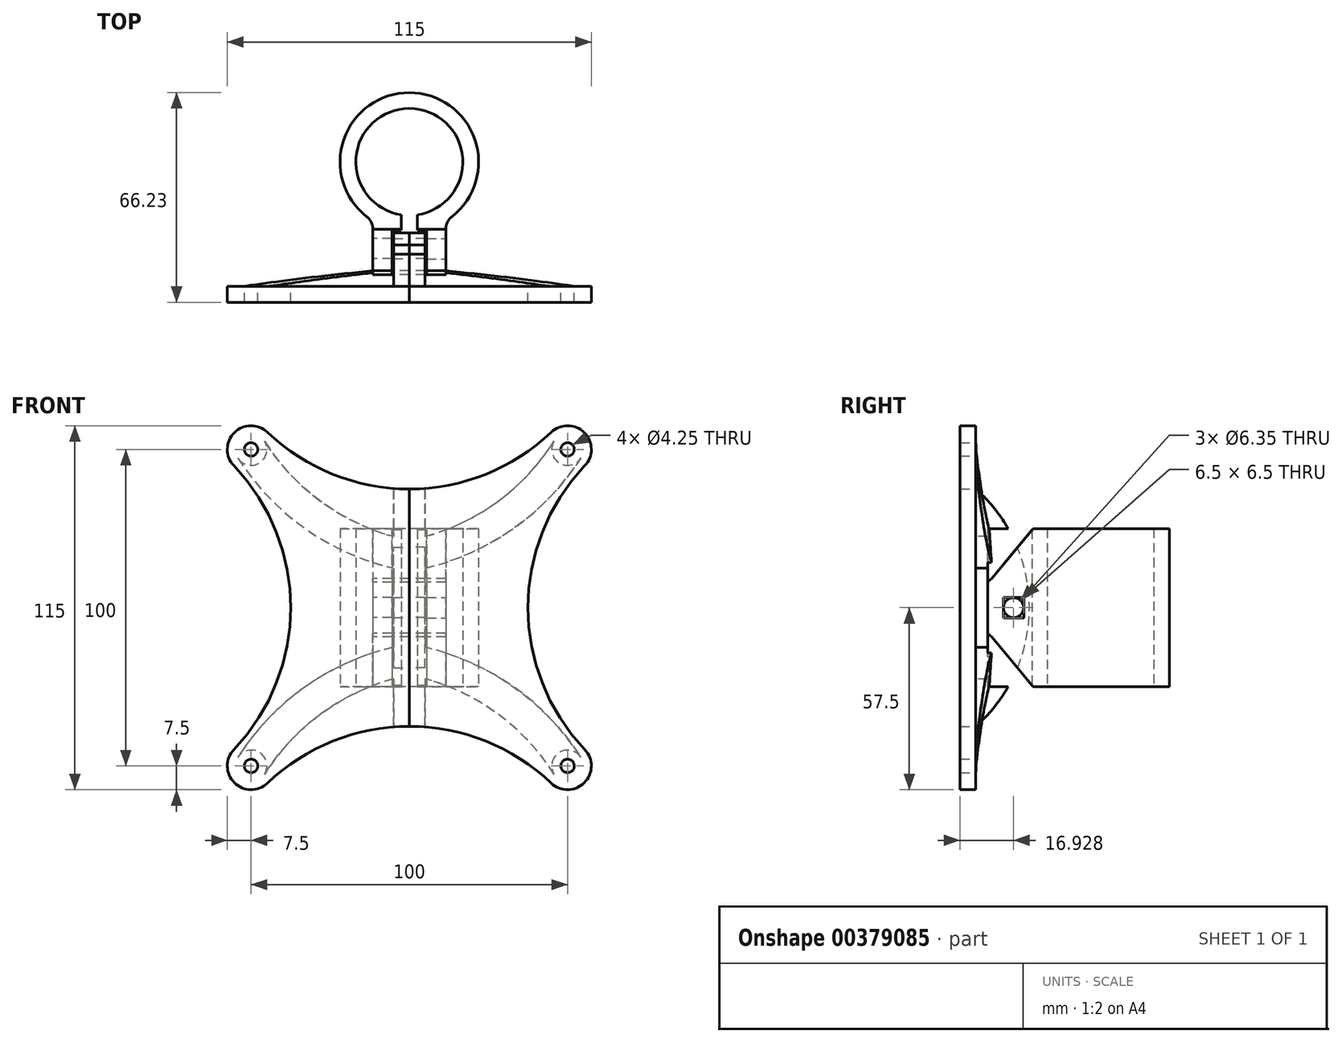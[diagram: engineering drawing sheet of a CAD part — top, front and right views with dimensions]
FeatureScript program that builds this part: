
annotation { "Feature Type Name" : "Feature", "Feature Type Description" : "" }
export const myFeature = defineFeature(function(context is Context, id is Id, definition is map)
    precondition{}
    {
        {
            var Q0;
            Q0=qCreatedBy(makeId("Front.planeOp"),FACE);
            var sketch = newSketch(context, id + "F0", { "sketchPlane" : qUnion([Q0])});
            skLineSegment(sketch, "E0.bottom", {"start": v(50, 50) * mm, "end": v(-50, 50) * mm, "construction": true});
            skLineSegment(sketch, "E0.top", {"start": v(50, -50) * mm, "end": v(-50, -50) * mm, "construction": true});
            skLineSegment(sketch, "E0.left", {"start": v(50, 50) * mm, "end": v(50, -50) * mm, "construction": true});
            skLineSegment(sketch, "E0.right", {"start": v(-50, 50) * mm, "end": v(-50, -50) * mm, "construction": true});
            skPoint(sketch, "E0.middle", {"position": v(0, 0) * mm});
            skCircle(sketch, "E1", {"center": v(-50, 50) * mm, "radius": 2.12 * mm});
            skCircle(sketch, "E2", {"center": v(50, 50) * mm, "radius": 2.12 * mm});
            skCircle(sketch, "E3", {"center": v(-50, -50) * mm, "radius": 2.12 * mm});
            skCircle(sketch, "E4", {"center": v(50, -50) * mm, "radius": 2.12 * mm});
            skArc(sketch, "E5", {"start": v(-44.83, 55.43) * mm, "mid": v(-55.3, 55.3) * mm, "end": v(-55.43, 44.83) * mm});
            skArc(sketch, "E6", {"start": v(55.43, 44.83) * mm, "mid": v(55.3, 55.3) * mm, "end": v(44.83, 55.43) * mm});
            skArc(sketch, "E7", {"start": v(44.83, -55.43) * mm, "mid": v(55.3, -55.3) * mm, "end": v(55.43, -44.83) * mm});
            skArc(sketch, "E8", {"start": v(-55.43, -44.83) * mm, "mid": v(-55.3, -55.3) * mm, "end": v(-44.83, -55.43) * mm});
            skLineSegment(sketch, "E9.bottom", {"start": v(37.5, 37.5) * mm, "end": v(-37.5, 37.5) * mm, "construction": true});
            skLineSegment(sketch, "E9.top", {"start": v(37.5, -37.5) * mm, "end": v(-37.5, -37.5) * mm, "construction": true});
            skLineSegment(sketch, "E9.left", {"start": v(37.5, 37.5) * mm, "end": v(37.5, -37.5) * mm, "construction": true});
            skLineSegment(sketch, "E9.right", {"start": v(-37.5, 37.5) * mm, "end": v(-37.5, -37.5) * mm, "construction": true});
            skArc(sketch, "E10", {"start": v(-44.83, 55.43) * mm, "mid": v(0, 37.5) * mm, "end": v(44.83, 55.43) * mm});
            skArc(sketch, "E11", {"start": v(44.83, -55.43) * mm, "mid": v(0, -37.5) * mm, "end": v(-44.83, -55.43) * mm});
            skArc(sketch, "E12", {"start": v(-55.43, -44.83) * mm, "mid": v(-37.5, 0) * mm, "end": v(-55.43, 44.83) * mm});
            skArc(sketch, "E13", {"start": v(55.43, 44.83) * mm, "mid": v(37.5, 0) * mm, "end": v(55.43, -44.83) * mm});
            skLineSegment(sketch, "E14", {"start": v(0, 37.5) * mm, "end": v(0, -37.5) * mm});
            skSolve(sketch);
        }
        {
            var Q0;
            Q0=makeQuery(id+"F0.imprint","IMPRINT",FACE,{"disambiguationData":[TD([[makeQuery(id+"F0.imprint","IMPRINT",EDGE,{"derivedFrom":sQuery(id+"F0.wireOp",EDGE,"E1")}),-1.0]])]});
            extrude(context, id + "F1", {"entities" : qUnion([Q0]), "depth" : 5 * mm, "offsetDistance" : 25 * mm});
        }
        {
            var Q0;
            Q0=qCreatedBy(makeId("Right.planeOp"),FACE);
            var sketch = newSketch(context, id + "F2", { "sketchPlane" : qUnion([Q0])});
            skLineSegment(sketch, "E15.0", {"start": v(0, 37.5) * mm, "end": v(0, -37.5) * mm});
            skArc(sketch, "E16", {"start": v(0, -37.5) * mm, "mid": v(16.93, 0) * mm, "end": v(0, 37.5) * mm});
            skLineSegment(sketch, "E17", {"start": v(0, 0) * mm, "end": v(16.93, 0) * mm, "construction": true});
            skCircle(sketch, "E18", {"center": v(11.93, 0) * mm, "radius": 3.17 * mm});
            skSolve(sketch);
        }
        {
            var Q0;
            Q0=makeQuery(id+"F2.imprint","IMPRINT",FACE,{"disambiguationData":[TD([[makeQuery(id+"F2.imprint","IMPRINT",EDGE,{"derivedFrom":sQuery(id+"F2.wireOp",EDGE,"E15.0")}),1.0]])]});
            extrude(context, id + "F3", {"entities" : qUnion([Q0]), "operationType" : NewBodyOperationType.ADD, "oppositeDirection" : true, "depth" : 5 * mm, "offsetDistance" : 25 * mm});
        }
        {
            var Q0;
            Q0=makeQuery(id+"F1.opExtrude","CAP_FACE",FACE,{"disambiguationData":[OSD([sQuery(id+"F0.wireOp",EDGE,"E1"),sQuery(id+"F0.wireOp",EDGE,"E3"),sQuery(id+"F0.wireOp",EDGE,"E5"),sQuery(id+"F0.wireOp",EDGE,"E8"),sQuery(id+"F0.wireOp",EDGE,"E10"),sQuery(id+"F0.wireOp",EDGE,"E11"),sQuery(id+"F0.wireOp",EDGE,"E12"),sQuery(id+"F0.wireOp",EDGE,"E14")])],"isStart":true});
            var sketch = newSketch(context, id + "F4", { "sketchPlane" : qUnion([Q0])});
            skCircle(sketch, "E19.0", {"center": v(50, 50) * mm, "radius": 2.13 * mm});
            skCircle(sketch, "E20.0", {"center": v(50, -50) * mm, "radius": 2.13 * mm});
            skLineSegment(sketch, "E21.0", {"start": v(5, 37.5) * mm, "end": v(5, -37.5) * mm});
            skCircle(sketch, "E22", {"center": v(50, 50) * mm, "radius": 5 * mm});
            skCircle(sketch, "E23", {"center": v(50, -50) * mm, "radius": 5 * mm});
            skArc(sketch, "E24", {"start": v(5, 22.5) * mm, "mid": v(28.21, 33.76) * mm, "end": v(45.77, 52.67) * mm});
            skArc(sketch, "E25", {"start": v(5, 12.5) * mm, "mid": v(33, 25.1) * mm, "end": v(54.21, 47.3) * mm});
            skArc(sketch, "E26", {"start": v(54.21, -47.3) * mm, "mid": v(33, -25.1) * mm, "end": v(5, -12.5) * mm});
            skArc(sketch, "E27", {"start": v(45.77, -52.67) * mm, "mid": v(28.21, -33.76) * mm, "end": v(5, -22.5) * mm});
            skSolve(sketch);
        }
        {
            var Q0;
            {var subQ0=sQuery(id+"F4.wireOp",EDGE,"E24");Q0=makeQuery(id+"F4.imprint","IMPRINT",FACE,{"disambiguationData":[TD([[makeQuery(id+"F4.imprint","IMPRINT",EDGE,{"derivedFrom":subQ0}),-1.0]])]});}
            var Q1;
            {var subQ0=sQuery(id+"F4.wireOp",EDGE,"E26");Q1=makeQuery(id+"F4.imprint","IMPRINT",FACE,{"disambiguationData":[TD([[makeQuery(id+"F4.imprint","IMPRINT",EDGE,{"derivedFrom":subQ0}),1.0]])]});}
            extrude(context, id + "F5", {"entities" : qUnion([Q0, Q1]), "operationType" : NewBodyOperationType.ADD, "depth" : 5 * mm, "offsetDistance" : 25 * mm});
        }
        {
            var Q0;
            Q0=makeQuery(id+"F5.opExtrude","CAP_EDGE",EDGE,{"disambiguationData":[OSD([sQuery(id+"F4.wireOp",EDGE,"E22")])],"isStart":false});
            chamfer(context, id + "F6", {"entities" : qUnion([Q0]), "chamferType" : ChamferType.TWO_OFFSETS, "width1" : 5 * mm, "oppositeDirection" : false, "width2" : 48 * mm, "tangentPropagation" : true});
        }
        {
            var Q0;
            Q0=makeQuery(id+"F5.opExtrude","CAP_EDGE",EDGE,{"disambiguationData":[OSD([sQuery(id+"F4.wireOp",EDGE,"E23")])],"isStart":false});
            chamfer(context, id + "F7", {"entities" : qUnion([Q0]), "chamferType" : ChamferType.TWO_OFFSETS, "width1" : 5 * mm, "oppositeDirection" : false, "width2" : 48 * mm, "tangentPropagation" : true});
        }
        {
            var Q0;
            Q0=makeQuery(id+"F1.opExtrude","SWEPT_BODY",BODY,{"disambiguationData":[OSD([sQuery(id+"F0.wireOp",EDGE,"E1"),sQuery(id+"F0.wireOp",EDGE,"E3"),sQuery(id+"F0.wireOp",EDGE,"E5"),sQuery(id+"F0.wireOp",EDGE,"E8"),sQuery(id+"F0.wireOp",EDGE,"E10"),sQuery(id+"F0.wireOp",EDGE,"E11"),sQuery(id+"F0.wireOp",EDGE,"E12"),sQuery(id+"F0.wireOp",EDGE,"E14")])]});
            var Q1;
            Q1=qCreatedBy(makeId("Right.planeOp"),FACE);
            mirror(context, id + "F8", {"entities" : qUnion([Q0]), "mirrorPlane" : qUnion([Q1])});
        }
        {
            var Q0;
            Q0=qCreatedBy(makeId("Top.planeOp"),FACE);
            var sketch = newSketch(context, id + "F9", { "sketchPlane" : qUnion([Q0])});
            skLineSegment(sketch, "E28.0", {"start": v(-5, 15.1) * mm, "end": v(-5, 8.75) * mm});
            skLineSegment(sketch, "E29.0", {"start": v(5, 15.1) * mm, "end": v(5, 8.75) * mm, "construction": true});
            skLineSegment(sketch, "E30.0.0", {"start": v(0, 0) * mm, "end": v(0, 16.93) * mm});
            skLineSegment(sketch, "E30.0.1", {"start": v(0, 0) * mm, "end": v(-5, 0) * mm, "construction": true});
            skLineSegment(sketch, "E30.0.2", {"start": v(-5, 0) * mm, "end": v(-5, 11.58) * mm});
            skLineSegment(sketch, "E30.0.3", {"start": v(-5, 11.58) * mm, "end": v(-5, 12) * mm});
            skLineSegment(sketch, "E30.0.4", {"start": v(-5, 12) * mm, "end": v(-5, 16.93) * mm, "construction": true});
            skLineSegment(sketch, "E30.0.5", {"start": v(-5, 11.58) * mm, "end": v(-5, 12) * mm, "construction": true});
            skLineSegment(sketch, "E30.0.6", {"start": v(-5, 0) * mm, "end": v(-5, 11.58) * mm, "construction": true});
            skLineSegment(sketch, "E30.0.7", {"start": v(-5, 0) * mm, "end": v(0, 0) * mm});
            skLineSegment(sketch, "E31.0.0", {"start": v(0, 0) * mm, "end": v(0, 16.93) * mm, "construction": true});
            skLineSegment(sketch, "E31.0.1", {"start": v(0, 0) * mm, "end": v(5, 0) * mm, "construction": true});
            skLineSegment(sketch, "E31.0.2", {"start": v(5, 0) * mm, "end": v(5, 11.58) * mm, "construction": true});
            skLineSegment(sketch, "E31.0.3", {"start": v(5, 11.58) * mm, "end": v(5, 12) * mm});
            skLineSegment(sketch, "E31.0.4", {"start": v(5, 12) * mm, "end": v(5, 16.93) * mm, "construction": true});
            skLineSegment(sketch, "E31.0.5", {"start": v(5, 11.58) * mm, "end": v(5, 12) * mm});
            skLineSegment(sketch, "E31.0.6", {"start": v(5, 0) * mm, "end": v(5, 11.58) * mm});
            skLineSegment(sketch, "E31.0.7", {"start": v(5, 0) * mm, "end": v(0, 0) * mm});
            skLineSegment(sketch, "E32", {"start": v(-5, 15.1) * mm, "end": v(5, 15.1) * mm, "construction": true});
            skLineSegment(sketch, "E33", {"start": v(-5, 8.75) * mm, "end": v(5, 8.75) * mm, "construction": true});
            skLineSegment(sketch, "E34", {"start": v(-5, 16.93) * mm, "end": v(5, 16.93) * mm, "construction": true});
            skArc(sketch, "E35", {"start": v(2.5, 22.61) * mm, "mid": v(0, 56.23) * mm, "end": v(-2.5, 22.61) * mm});
            skArc(sketch, "E36", {"start": v(13.43, 22.03) * mm, "mid": v(0, 61.23) * mm, "end": v(-13.43, 22.03) * mm});
            skLineSegment(sketch, "E37", {"start": v(-5.5, 17.75) * mm, "end": v(-5.5, 3.75) * mm});
            skLineSegment(sketch, "E38", {"start": v(-5.5, 3.75) * mm, "end": v(-11.5, 3.75) * mm});
            skLineSegment(sketch, "E39", {"start": v(-11.5, 3.75) * mm, "end": v(-11.5, 18.08) * mm});
            skLineSegment(sketch, "E40", {"start": v(0, 16.93) * mm, "end": v(0, 61.73) * mm, "construction": true});
            skLineSegment(sketch, "E41.MirrorCS", {"start": v(5.5, 17.75) * mm, "end": v(5.5, 3.75) * mm});
            skLineSegment(sketch, "E42.MirrorCS", {"start": v(11.5, 3.75) * mm, "end": v(11.5, 18.08) * mm});
            skLineSegment(sketch, "E43.MirrorCS", {"start": v(5.5, 3.75) * mm, "end": v(11.5, 3.75) * mm});
            skPoint(sketch, "E44.visualSharp", {"position": v(-11.5, 20.7) * mm});
            skArc(sketch, "E44.filletArc", {"start": v(-11.5, 18.08) * mm, "mid": v(-12, 20.28) * mm, "end": v(-13.43, 22.03) * mm});
            skPoint(sketch, "E45.visualSharp", {"position": v(11.5, 20.7) * mm});
            skArc(sketch, "E45.filletArc", {"start": v(13.43, 22.03) * mm, "mid": v(12, 20.28) * mm, "end": v(11.5, 18.08) * mm});
            skLineSegment(sketch, "E46", {"start": v(-5.5, 17.75) * mm, "end": v(-2.5, 17.75) * mm});
            skLineSegment(sketch, "E47", {"start": v(-2.5, 22.61) * mm, "end": v(-2.5, 17.75) * mm});
            skLineSegment(sketch, "E48", {"start": v(2.5, 22.61) * mm, "end": v(2.5, 17.75) * mm});
            skPoint(sketch, "E49.orphan", {"position": v(-5.5, 23.35) * mm});
            skPoint(sketch, "E50.orphan", {"position": v(5.5, 23.35) * mm});
            skLineSegment(sketch, "E51.trimOffspring", {"start": v(2.5, 17.75) * mm, "end": v(5.5, 17.75) * mm});
            skSolve(sketch);
        }
        {
            var Q0;
            Q0=makeQuery(id+"F9.imprint","IMPRINT",FACE,{"disambiguationData":[TD([[makeQuery(id+"F9.imprint","IMPRINT",EDGE,{"derivedFrom":sQuery(id+"F9.wireOp",EDGE,"E35")}),-1.0]])]});
            extrude(context, id + "F10", {"entities" : qUnion([Q0]), "endBound" : BoundingType.SYMMETRIC, "depth" : 50 * mm, "offsetDistance" : 25 * mm});
        }
        {
            var Q0;
            Q0=makeQuery(id+"F10.opExtrude","SWEPT_FACE",FACE,{"disambiguationData":[OSD([sQuery(id+"F9.wireOp",EDGE,"E39")])]});
            var sketch = newSketch(context, id + "F11", { "sketchPlane" : qUnion([Q0])});
            skCircle(sketch, "E52.0", {"center": v(-11.93, 0) * mm, "radius": 3.18 * mm});
            skLineSegment(sketch, "E53.0", {"start": v(-5, 12.5) * mm, "end": v(0, 12.5) * mm, "construction": true});
            skLineSegment(sketch, "E54.0", {"start": v(-5, -12.5) * mm, "end": v(0, -12.5) * mm, "construction": true});
            skLineSegment(sketch, "E55.0", {"start": v(0, 12.5) * mm, "end": v(0, -12.5) * mm, "construction": true});
            skCircle(sketch, "E56", {"center": v(-11.93, 0) * mm, "radius": 11.5 * mm});
            skLineSegment(sketch, "E57.0", {"start": v(-18.08, 25) * mm, "end": v(-18.08, -25) * mm});
            skLineSegment(sketch, "E58", {"start": v(-5, -12.5) * mm, "end": v(-5, 12.5) * mm, "construction": true});
            skLineSegment(sketch, "E59", {"start": v(-18.08, -25) * mm, "end": v(-5, -9.18) * mm});
            skLineSegment(sketch, "E60", {"start": v(-18.08, 25) * mm, "end": v(-5, 9.18) * mm});
            skLineSegment(sketch, "E61.0", {"start": v(-3.75, -25) * mm, "end": v(-18.08, -25) * mm});
            skLineSegment(sketch, "E62.0", {"start": v(-3.75, 25) * mm, "end": v(-3.75, -25) * mm});
            skLineSegment(sketch, "E63.0", {"start": v(-3.75, 25) * mm, "end": v(-18.08, 25) * mm});
            skLineSegment(sketch, "E64", {"start": v(-5, 12.5) * mm, "end": v(-11.93, 12.5) * mm, "construction": true});
            skLineSegment(sketch, "E65", {"start": v(-11.93, 12.5) * mm, "end": v(-11.93, -12.5) * mm, "construction": true});
            skLineSegment(sketch, "E66", {"start": v(-11.93, -12.5) * mm, "end": v(-5, -12.5) * mm, "construction": true});
            skSolve(sketch);
        }
        {
            var Q0;
            {var subQ0=sQuery(id+"F11.wireOp",EDGE,"E60");Q0=makeQuery(id+"F11.imprint","IMPRINT",FACE,{"disambiguationData":[TD([[makeQuery(id+"F11.imprint","IMPRINT",EDGE,{"derivedFrom":subQ0}),1.0]])]});}
            var Q1;
            {var subQ0=sQuery(id+"F11.wireOp",EDGE,"E59");Q1=makeQuery(id+"F11.imprint","IMPRINT",FACE,{"disambiguationData":[TD([[makeQuery(id+"F11.imprint","IMPRINT",EDGE,{"derivedFrom":subQ0}),-1.0]])]});}
            var Q2;
            Q2=makeQuery(id+"F11.imprint","IMPRINT",FACE,{"disambiguationData":[TD([[makeQuery(id+"F11.imprint","IMPRINT",EDGE,{"derivedFrom":sQuery(id+"F11.wireOp",EDGE,"E52.0")}),1.0]])]});
            var Q3;
            Q3=makeQuery(id+"F10.opExtrude","SWEPT_FACE",FACE,{"disambiguationData":[OSD([sQuery(id+"F9.wireOp",EDGE,"E42.MirrorCS")])]});
            extrude(context, id + "F12", {"entities" : qUnion([Q0, Q1, Q2]), "operationType" : NewBodyOperationType.REMOVE, "endBound" : BoundingType.UP_TO_SURFACE, "oppositeDirection" : true, "depth" : 25 * mm, "endBoundEntityFace" : qUnion([Q3]), "offsetDistance" : 25 * mm});
        }
        {
            var Q0;
            Q0=makeQuery(id+"F10.opExtrude","SWEPT_FACE",FACE,{"disambiguationData":[OSD([sQuery(id+"F9.wireOp",EDGE,"E42.MirrorCS")])]});
            var sketch = newSketch(context, id + "F13", { "sketchPlane" : qUnion([Q0])});
            skCircle(sketch, "E67.0", {"center": v(11.93, 0) * mm, "radius": 3.18 * mm, "construction": true});
            skLineSegment(sketch, "E68.bottom", {"start": v(15.18, -3.25) * mm, "end": v(8.68, -3.25) * mm});
            skLineSegment(sketch, "E68.top", {"start": v(15.18, 3.25) * mm, "end": v(8.68, 3.25) * mm});
            skLineSegment(sketch, "E68.left", {"start": v(15.18, -3.25) * mm, "end": v(15.18, 3.25) * mm});
            skLineSegment(sketch, "E68.right", {"start": v(8.68, -3.25) * mm, "end": v(8.68, 3.25) * mm});
            skSolve(sketch);
        }
        {
            var Q0;
            Q0=makeQuery(id+"F13.imprint","IMPRINT",FACE,{"disambiguationData":[TD([[makeQuery(id+"F13.imprint","IMPRINT",EDGE,{"derivedFrom":sQuery(id+"F13.wireOp",EDGE,"E68.bottom")}),-1.0]])]});
            extrude(context, id + "F14", {"entities" : qUnion([Q0]), "operationType" : NewBodyOperationType.REMOVE, "oppositeDirection" : true, "depth" : 6 * mm, "offsetDistance" : 25 * mm});
        }
    });
